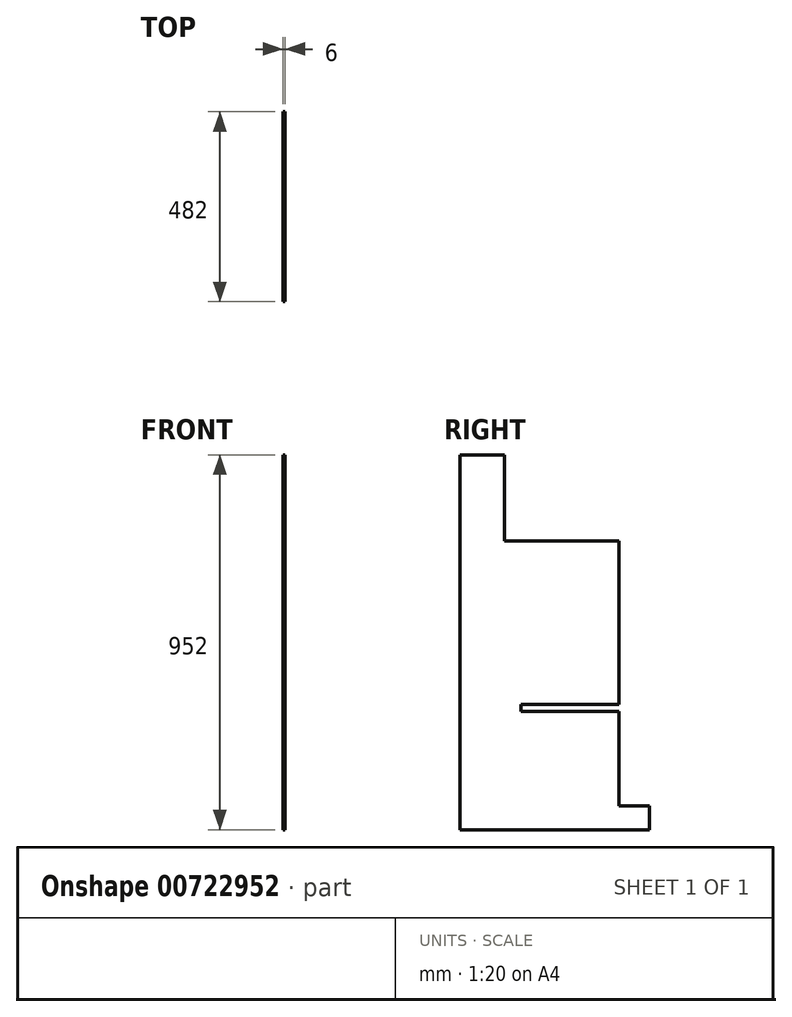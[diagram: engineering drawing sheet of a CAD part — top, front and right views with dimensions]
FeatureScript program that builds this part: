
annotation { "Feature Type Name" : "Feature", "Feature Type Description" : "" }
export const myFeature = defineFeature(function(context is Context, id is Id, definition is map)
    precondition{}
    {
        {
            var Q0;
            Q0=qCreatedBy(makeId("Right.planeOp"),FACE);
            var sketch = newSketch(context, id + "F0", { "sketchPlane" : qUnion([Q0])});
            skLineSegment(sketch, "E0.bottom", {"start": v(-482, 218) * mm, "end": v(-368, 218) * mm});
            skLineSegment(sketch, "E0.top", {"start": v(-482, -734) * mm, "end": v(0, -734) * mm});
            skLineSegment(sketch, "E0.left", {"start": v(-482, 218) * mm, "end": v(-482, -734) * mm});
            skLineSegment(sketch, "E0.right", {"start": v(0, -674) * mm, "end": v(0, -734) * mm});
            skLineSegment(sketch, "E1", {"start": v(-368, 218) * mm, "end": v(-368, 0) * mm});
            skLineSegment(sketch, "E2", {"start": v(-368, 0) * mm, "end": v(-78, 0) * mm});
            skLineSegment(sketch, "E3", {"start": v(-78, 0) * mm, "end": v(-78, -416) * mm});
            skLineSegment(sketch, "E4", {"start": v(-78, -416) * mm, "end": v(-326, -416) * mm});
            skLineSegment(sketch, "E5", {"start": v(-326, -416) * mm, "end": v(-326, -434) * mm});
            skLineSegment(sketch, "E6", {"start": v(-326, -434) * mm, "end": v(-78, -434) * mm});
            skLineSegment(sketch, "E7", {"start": v(-78, -434) * mm, "end": v(-78, -674) * mm});
            skLineSegment(sketch, "E8", {"start": v(-78, -674) * mm, "end": v(-60, -674) * mm});
            skLineSegment(sketch, "E9", {"start": v(-60, -674) * mm, "end": v(0, -674) * mm});
            skSolve(sketch);
        }
        {
            var Q0;
            Q0 = qSketchRegion(id + "F0", true);
            extrude(context, id + "F1", {"entities" : qUnion([Q0]), "depth" : 6 * mm, "offsetDistance" : 25 * mm});
        }
    });
